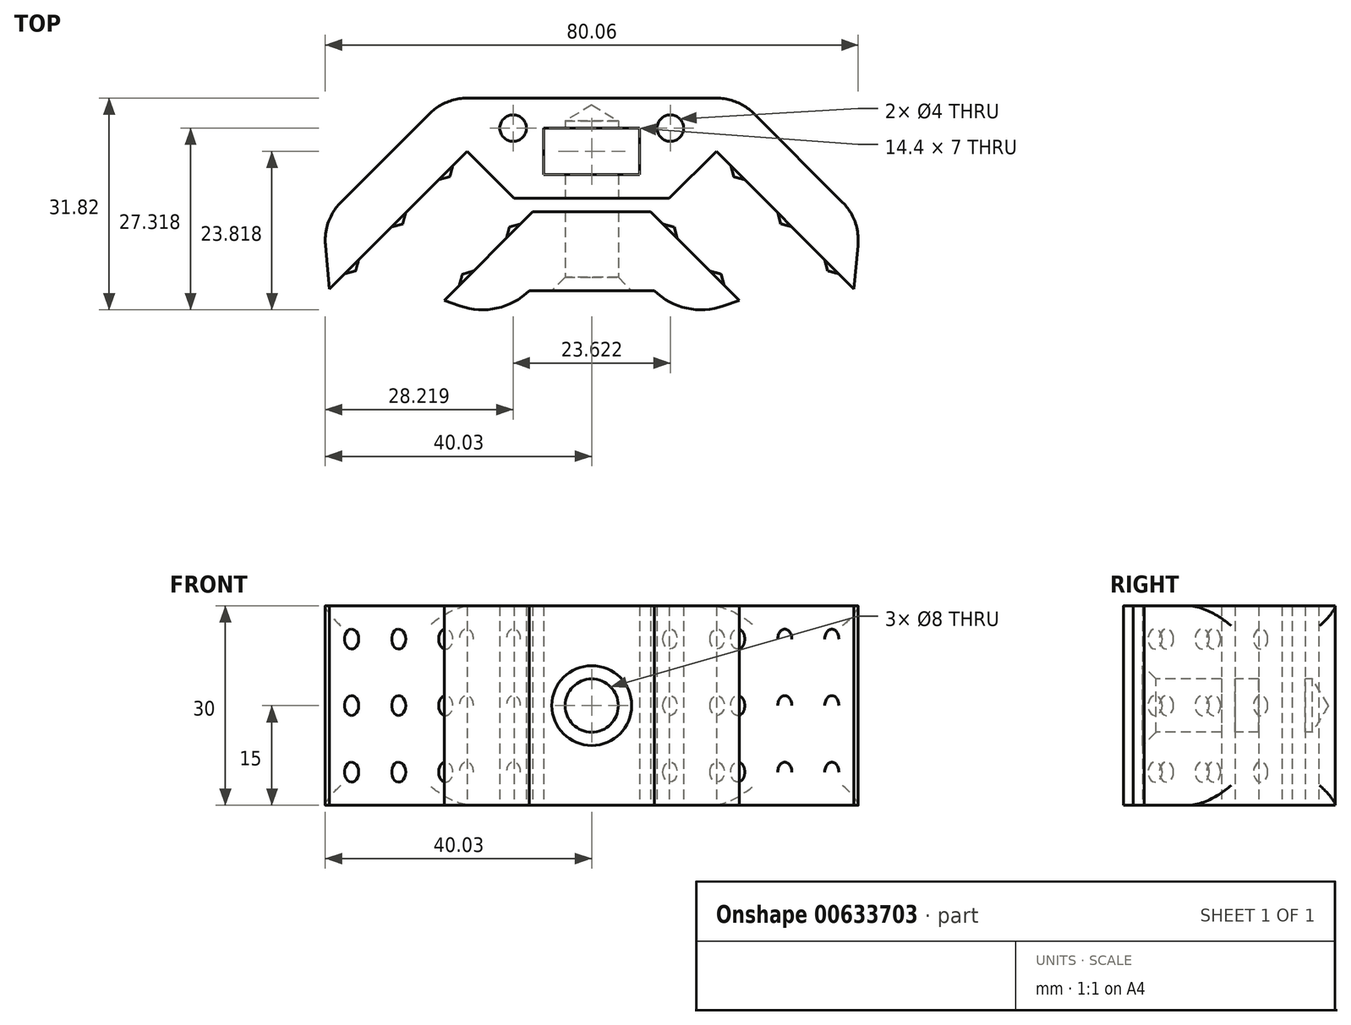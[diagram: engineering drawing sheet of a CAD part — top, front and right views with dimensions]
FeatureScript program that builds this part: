
annotation { "Feature Type Name" : "Feature", "Feature Type Description" : "" }
export const myFeature = defineFeature(function(context is Context, id is Id, definition is map)
    precondition{}
    {
        {
            var Q0;
            Q0=qCreatedBy(makeId("Top.planeOp"),FACE);
            var sketch = newSketch(context, id + "F0", { "sketchPlane" : qUnion([Q0])});
            skLineSegment(sketch, "E0", {"start": v(-6, 0) * mm, "end": v(6, 0) * mm, "construction": true});
            skLineSegment(sketch, "E1.bottom", {"start": v(6, 0) * mm, "end": v(8.87, -2.87) * mm, "construction": true});
            skLineSegment(sketch, "E1.top", {"start": v(18.73, 12.73) * mm, "end": v(89.44, -57.98) * mm});
            skLineSegment(sketch, "E1.left", {"start": v(6, 0) * mm, "end": v(11.66, 5.66) * mm, "construction": true});
            skLineSegment(sketch, "E2.bottom", {"start": v(-6, 0) * mm, "end": v(-8.87, -2.87) * mm, "construction": true});
            skLineSegment(sketch, "E2.top", {"start": v(-18.73, 12.73) * mm, "end": v(-89.44, -57.98) * mm});
            skLineSegment(sketch, "E2.left", {"start": v(-6, 0) * mm, "end": v(-11.66, 5.66) * mm, "construction": true});
            skLineSegment(sketch, "E3", {"start": v(0, 0) * mm, "end": v(0, 18.24) * mm, "construction": true});
            skLineSegment(sketch, "E4", {"start": v(-18.73, 12.73) * mm, "end": v(18.73, 12.73) * mm, "construction": true});
            skLineSegment(sketch, "E5.0", {"start": v(22.04, 20.73) * mm, "end": v(95.1, -52.33) * mm});
            skLineSegment(sketch, "E5.1", {"start": v(-22.04, 20.73) * mm, "end": v(22.04, 20.73) * mm});
            skLineSegment(sketch, "E5.2", {"start": v(-22.04, 20.73) * mm, "end": v(-95.1, -52.33) * mm});
            skPoint(sketch, "E6", {"position": v(-40.34, 2.43) * mm});
            skLineSegment(sketch, "E7", {"start": v(-40.34, 2.43) * mm, "end": v(-39.4, -7.94) * mm});
            skLineSegment(sketch, "E8.MirrorCS", {"start": v(40.34, 2.43) * mm, "end": v(39.4, -7.94) * mm});
            skLineSegment(sketch, "E9.0", {"start": v(-2.69, -8) * mm, "end": v(-71.05, -76.37) * mm});
            skLineSegment(sketch, "E9.1", {"start": v(-2.69, -8) * mm, "end": v(2.69, -8) * mm});
            skLineSegment(sketch, "E9.2", {"start": v(2.69, -8) * mm, "end": v(71.05, -76.37) * mm});
            skLineSegment(sketch, "E10", {"start": v(-22.15, -16.15) * mm, "end": v(-13.82, -19.13) * mm});
            skLineSegment(sketch, "E11.MirrorCS", {"start": v(22.15, -16.15) * mm, "end": v(13.82, -19.13) * mm});
            skLineSegment(sketch, "E12", {"start": v(-9.38, -14.7) * mm, "end": v(9.38, -14.7) * mm});
            skLineSegment(sketch, "E13", {"start": v(-11.66, 5.66) * mm, "end": v(11.66, 5.66) * mm});
            skLineSegment(sketch, "E14", {"start": v(-8.87, -2.87) * mm, "end": v(8.87, -2.87) * mm});
            skLineSegment(sketch, "E15.bottom", {"start": v(7.2, 16.23) * mm, "end": v(-7.2, 16.23) * mm});
            skLineSegment(sketch, "E15.top", {"start": v(7.2, 9.23) * mm, "end": v(-7.2, 9.23) * mm});
            skLineSegment(sketch, "E15.left", {"start": v(7.2, 16.23) * mm, "end": v(7.2, 9.23) * mm});
            skLineSegment(sketch, "E15.right", {"start": v(-7.2, 16.23) * mm, "end": v(-7.2, 9.23) * mm});
            skPoint(sketch, "E15.middle", {"position": v(0, 12.73) * mm});
            skCircle(sketch, "E16", {"center": v(-11.81, 16.23) * mm, "radius": 2 * mm});
            skCircle(sketch, "E17.MirrorC", {"center": v(11.81, 16.23) * mm, "radius": 2 * mm});
            skLineSegment(sketch, "E18", {"start": v(-11.66, 5.66) * mm, "end": v(-18.73, 12.73) * mm});
            skLineSegment(sketch, "E19", {"start": v(-8.87, -2.87) * mm, "end": v(-76.71, -70.71) * mm});
            skLineSegment(sketch, "E20", {"start": v(8.87, -2.87) * mm, "end": v(76.71, -70.71) * mm});
            skLineSegment(sketch, "E21", {"start": v(11.66, 5.66) * mm, "end": v(18.73, 12.73) * mm});
            skSolve(sketch);
        }
        {
            var Q0;
            {var subQ9=sQuery(id+"F0.wireOp",EDGE,"E5.1");Q0=makeQuery(id+"F0.imprint","IMPRINT",FACE,{"disambiguationData":[TD([[makeQuery(id+"F0.imprint","IMPRINT",EDGE,{"derivedFrom":subQ9}),-1.0]])]});}
            var Q1;
            {var subQ0=sQuery(id+"F0.wireOp",EDGE,"E10");Q1=makeQuery(id+"F0.imprint","IMPRINT",FACE,{"disambiguationData":[TD([[makeQuery(id+"F0.imprint","IMPRINT",EDGE,{"derivedFrom":subQ0}),1.0]])]});}
            var Q2;
            {var subQ0=sQuery(id+"F0.wireOp",EDGE,"E9.1");Q2=makeQuery(id+"F0.imprint","IMPRINT",FACE,{"disambiguationData":[TD([[makeQuery(id+"F0.imprint","IMPRINT",EDGE,{"derivedFrom":subQ0}),-1.0]])]});}
            extrude(context, id + "F1", {"entities" : qUnion([Q0, Q1, Q2]), "depth" : 30 * mm, "offsetDistance" : 25 * mm});
        }
        {
            var Q0;
            Q0=makeQuery(id+"F1.opExtrude","SWEPT_FACE",FACE,{"disambiguationData":[OSD([sQuery(id+"F0.wireOp",EDGE,"E12")])]});
            var sketch = newSketch(context, id + "F2", { "sketchPlane" : qUnion([Q0])});
            skPoint(sketch, "E22", {"position": v(0, 15) * mm});
            skPoint(sketch, "E22.positionSnap0", {"position": v(0, 30) * mm});
            skPoint(sketch, "E22.positionSnap1", {"position": v(-9.38, 15) * mm});
            skSolve(sketch);
        }
        {
            var Q0;
            Q0=sQuery(id+"F2.wireOp",VERTEX,"E22");
            var Q1;
            Q1=makeQuery(id+"F1.opExtrude","SWEPT_BODY",BODY,{"disambiguationData":[OSD([sQuery(id+"F0.wireOp",EDGE,"E1.top"),sQuery(id+"F0.wireOp",EDGE,"E2.top"),sQuery(id+"F0.wireOp",EDGE,"E5.0"),sQuery(id+"F0.wireOp",EDGE,"E5.1"),sQuery(id+"F0.wireOp",EDGE,"E5.2"),sQuery(id+"F0.wireOp",EDGE,"E7"),sQuery(id+"F0.wireOp",EDGE,"E8.MirrorCS"),sQuery(id+"F0.wireOp",EDGE,"E13"),sQuery(id+"F0.wireOp",EDGE,"E15.bottom"),sQuery(id+"F0.wireOp",EDGE,"E15.top"),sQuery(id+"F0.wireOp",EDGE,"E15.left"),sQuery(id+"F0.wireOp",EDGE,"E15.right"),sQuery(id+"F0.wireOp",EDGE,"E16"),sQuery(id+"F0.wireOp",EDGE,"E17.MirrorC"),sQuery(id+"F0.wireOp",EDGE,"E18"),sQuery(id+"F0.wireOp",EDGE,"E21")])]});
            var Q2;
            Q2=makeQuery(id+"F1.opExtrude","SWEPT_BODY",BODY,{"disambiguationData":[OSD([sQuery(id+"F0.wireOp",EDGE,"E9.0"),sQuery(id+"F0.wireOp",EDGE,"E9.2"),sQuery(id+"F0.wireOp",EDGE,"E10"),sQuery(id+"F0.wireOp",EDGE,"E11.MirrorCS"),sQuery(id+"F0.wireOp",EDGE,"E12"),sQuery(id+"F0.wireOp",EDGE,"E14"),sQuery(id+"F0.wireOp",EDGE,"E19"),sQuery(id+"F0.wireOp",EDGE,"E20")])]});
            hole(context, id + "F3", {"style" : HoleStyle.C_SINK, "endStyle" : HoleEndStyle.BLIND, "holeDiameter" : 8 * mm, "cSinkDiameter" : 12 * mm, "cSinkAngle" : 90 * degree, "majorDiameter" : 5 * mm, "holeDepth" : 32 * mm, "isTappedThrough" : true, "tappedDepth" : 12 * mm, "tapClearance" : 3, "startFromSketch" : true, "locations" : qUnion([Q0]), "scope" : qUnion([Q1, Q2])});
        }
        {
            var Q0;
            Q0=makeQuery(id+"F1.opExtrude","SWEPT_EDGE",EDGE,{"disambiguationData":[OSD([sQuery(id+"F0.wireOp",EDGE,"E5.2"),sQuery(id+"F0.wireOp",EDGE,"E7")])]});
            var Q1;
            Q1=makeQuery(id+"F1.opExtrude","SWEPT_EDGE",EDGE,{"disambiguationData":[OSD([sQuery(id+"F0.wireOp",EDGE,"E5.1"),sQuery(id+"F0.wireOp",EDGE,"E5.2")])]});
            var Q2;
            Q2=makeQuery(id+"F1.opExtrude","SWEPT_EDGE",EDGE,{"disambiguationData":[OSD([sQuery(id+"F0.wireOp",EDGE,"E5.0"),sQuery(id+"F0.wireOp",EDGE,"E5.1")])]});
            var Q3;
            Q3=makeQuery(id+"F1.opExtrude","SWEPT_EDGE",EDGE,{"disambiguationData":[OSD([sQuery(id+"F0.wireOp",EDGE,"E5.0"),sQuery(id+"F0.wireOp",EDGE,"E8.MirrorCS")])]});
            fillet(context, id + "F4", {"entities" : qUnion([Q0, Q1, Q2, Q3]), "radius" : 8 * mm, "tangentPropagation" : true, "allowEdgeOverflow" : false});
        }
        {
            var Q0;
            Q0=makeQuery(id+"F1.opExtrude","CAP_EDGE",EDGE,{"disambiguationData":[OSD([sQuery(id+"F0.wireOp",EDGE,"E5.0")])],"isStart":false});
            var Q1;
            Q1=makeQuery(id+"F1.opExtrude","CAP_EDGE",EDGE,{"disambiguationData":[OSD([sQuery(id+"F0.wireOp",EDGE,"E5.2")])],"isStart":false});
            var Q2;
            Q2=makeQuery(id+"F1.opExtrude","CAP_EDGE",EDGE,{"disambiguationData":[OSD([sQuery(id+"F0.wireOp",EDGE,"E5.0")])],"isStart":true});
            var Q3;
            Q3=makeQuery(id+"F1.opExtrude","CAP_EDGE",EDGE,{"disambiguationData":[OSD([sQuery(id+"F0.wireOp",EDGE,"E5.2")])],"isStart":true});
            fillet(context, id + "F5", {"entities" : qUnion([Q0, Q1, Q2, Q3]), "radius" : 3 * mm, "allowEdgeOverflow" : false});
        }
        {
            var Q0;
            Q0=makeQuery(id+"F1.opExtrude","SWEPT_EDGE",EDGE,{"disambiguationData":[OSD([sQuery(id+"F0.wireOp",EDGE,"E9.0"),sQuery(id+"F0.wireOp",EDGE,"E10")])]});
            var Q1;
            Q1=makeQuery(id+"F1.opExtrude","SWEPT_EDGE",EDGE,{"disambiguationData":[OSD([sQuery(id+"F0.wireOp",EDGE,"E9.2"),sQuery(id+"F0.wireOp",EDGE,"E11.MirrorCS")])]});
            fillet(context, id + "F6", {"entities" : qUnion([Q0, Q1]), "radius" : 10 * mm, "tangentPropagation" : true, "allowEdgeOverflow" : false});
        }
        {
            var Q0;
            Q0=makeQuery(id+"F1.opExtrude","SWEPT_FACE",FACE,{"disambiguationData":[OSD([sQuery(id+"F0.wireOp",EDGE,"E2.top")])]});
            var sketch = newSketch(context, id + "F7", { "sketchPlane" : qUnion([Q0])});
            skCircle(sketch, "E23", {"center": v(-28.78, 25) * mm, "radius": 1.5 * mm});
            skCircle(sketch, "E24.0.1.0", {"center": v(-28.78, 15) * mm, "radius": 1.5 * mm});
            skCircle(sketch, "E24.0.2.0", {"center": v(-28.78, 5) * mm, "radius": 1.5 * mm});
            skCircle(sketch, "E24.1.0.0", {"center": v(-18.78, 25) * mm, "radius": 1.5 * mm});
            skCircle(sketch, "E24.1.1.0", {"center": v(-18.78, 15) * mm, "radius": 1.5 * mm});
            skCircle(sketch, "E24.1.2.0", {"center": v(-18.78, 5) * mm, "radius": 1.5 * mm});
            skCircle(sketch, "E24.2.0.0", {"center": v(-8.78, 25) * mm, "radius": 1.5 * mm});
            skCircle(sketch, "E24.2.1.0", {"center": v(-8.78, 15) * mm, "radius": 1.5 * mm});
            skCircle(sketch, "E24.2.2.0", {"center": v(-8.78, 5) * mm, "radius": 1.5 * mm});
            skLineSegment(sketch, "E24.direction1", {"start": v(-28.78, 25) * mm, "end": v(-18.78, 25) * mm, "construction": true});
            skLineSegment(sketch, "E24.direction2", {"start": v(-28.78, 25) * mm, "end": v(-28.78, 15) * mm, "construction": true});
            skLineSegment(sketch, "E25", {"start": v(-28.78, 25) * mm, "end": v(-33.48, 25) * mm, "construction": true});
            skLineSegment(sketch, "E26", {"start": v(-28.78, 25) * mm, "end": v(-28.78, 30) * mm, "construction": true});
            skSolve(sketch);
        }
        {
            var Q0;
            Q0=makeQuery(id+"F1.opExtrude","SWEPT_FACE",FACE,{"disambiguationData":[OSD([sQuery(id+"F0.wireOp",EDGE,"E1.top")])]});
            var sketch = newSketch(context, id + "F8", { "sketchPlane" : qUnion([Q0])});
            skCircle(sketch, "E27", {"center": v(8.78, 25) * mm, "radius": 1.5 * mm});
            skCircle(sketch, "E28.0.1.0", {"center": v(8.78, 15) * mm, "radius": 1.5 * mm});
            skCircle(sketch, "E28.0.2.0", {"center": v(8.78, 5) * mm, "radius": 1.5 * mm});
            skCircle(sketch, "E28.1.0.0", {"center": v(18.78, 25) * mm, "radius": 1.5 * mm});
            skCircle(sketch, "E28.1.1.0", {"center": v(18.78, 15) * mm, "radius": 1.5 * mm});
            skCircle(sketch, "E28.1.2.0", {"center": v(18.78, 5) * mm, "radius": 1.5 * mm});
            skCircle(sketch, "E28.2.0.0", {"center": v(28.78, 25) * mm, "radius": 1.5 * mm});
            skCircle(sketch, "E28.2.1.0", {"center": v(28.78, 15) * mm, "radius": 1.5 * mm});
            skCircle(sketch, "E28.2.2.0", {"center": v(28.78, 5) * mm, "radius": 1.5 * mm});
            skLineSegment(sketch, "E28.direction1", {"start": v(8.78, 25) * mm, "end": v(18.78, 25) * mm, "construction": true});
            skLineSegment(sketch, "E28.direction2", {"start": v(8.78, 25) * mm, "end": v(8.78, 15) * mm, "construction": true});
            skLineSegment(sketch, "E29", {"start": v(28.78, 25) * mm, "end": v(33.48, 25) * mm, "construction": true});
            skLineSegment(sketch, "E30", {"start": v(33.48, 25) * mm, "end": v(28.78, 25) * mm, "construction": true});
            skLineSegment(sketch, "E31", {"start": v(28.78, 25) * mm, "end": v(28.78, 30) * mm, "construction": true});
            skSolve(sketch);
        }
        {
            var Q0;
            Q0=makeQuery(id+"F1.opExtrude","SWEPT_FACE",FACE,{"disambiguationData":[OSD([sQuery(id+"F0.wireOp",EDGE,"E19")])]});
            var sketch = newSketch(context, id + "F9", { "sketchPlane" : qUnion([Q0])});
            skCircle(sketch, "E32", {"center": v(12.39, 25) * mm, "radius": 1.5 * mm});
            skCircle(sketch, "E33.0.1.0", {"center": v(12.39, 15) * mm, "radius": 1.5 * mm});
            skCircle(sketch, "E33.0.2.0", {"center": v(12.39, 5) * mm, "radius": 1.5 * mm});
            skCircle(sketch, "E33.1.0.0", {"center": v(22.39, 25) * mm, "radius": 1.5 * mm});
            skCircle(sketch, "E33.1.1.0", {"center": v(22.39, 15) * mm, "radius": 1.5 * mm});
            skCircle(sketch, "E33.1.2.0", {"center": v(22.39, 5) * mm, "radius": 1.5 * mm});
            skLineSegment(sketch, "E33.direction1", {"start": v(12.39, 25) * mm, "end": v(22.39, 25) * mm, "construction": true});
            skLineSegment(sketch, "E33.direction2", {"start": v(12.39, 25) * mm, "end": v(12.39, 15) * mm, "construction": true});
            skLineSegment(sketch, "E34", {"start": v(22.39, 25) * mm, "end": v(22.39, 30) * mm, "construction": true});
            skLineSegment(sketch, "E35", {"start": v(22.39, 25) * mm, "end": v(27.09, 25) * mm, "construction": true});
            skSolve(sketch);
        }
        {
            var Q0;
            Q0=makeQuery(id+"F1.opExtrude","SWEPT_FACE",FACE,{"disambiguationData":[OSD([sQuery(id+"F0.wireOp",EDGE,"E20")])]});
            var sketch = newSketch(context, id + "F10", { "sketchPlane" : qUnion([Q0])});
            skCircle(sketch, "E36", {"center": v(-22.39, 25) * mm, "radius": 1.5 * mm});
            skCircle(sketch, "E37.0.1.0", {"center": v(-22.39, 15) * mm, "radius": 1.5 * mm});
            skCircle(sketch, "E37.0.2.0", {"center": v(-22.39, 5) * mm, "radius": 1.5 * mm});
            skCircle(sketch, "E37.1.0.0", {"center": v(-12.39, 25) * mm, "radius": 1.5 * mm});
            skCircle(sketch, "E37.1.1.0", {"center": v(-12.39, 15) * mm, "radius": 1.5 * mm});
            skCircle(sketch, "E37.1.2.0", {"center": v(-12.39, 5) * mm, "radius": 1.5 * mm});
            skLineSegment(sketch, "E37.direction1", {"start": v(-22.39, 25) * mm, "end": v(-12.39, 25) * mm, "construction": true});
            skLineSegment(sketch, "E37.direction2", {"start": v(-22.39, 25) * mm, "end": v(-22.39, 15) * mm, "construction": true});
            skLineSegment(sketch, "E38", {"start": v(-22.39, 25) * mm, "end": v(-27.09, 25) * mm});
            skLineSegment(sketch, "E39", {"start": v(-27.09, 25) * mm, "end": v(-22.39, 25) * mm, "construction": true});
            skLineSegment(sketch, "E40", {"start": v(-22.39, 25) * mm, "end": v(-22.39, 30) * mm, "construction": true});
            skSolve(sketch);
        }
        {
            var Q0;
            Q0 = qSketchRegion(id + "F9", true);
            extrude(context, id + "F11", {"entities" : qUnion([Q0]), "operationType" : NewBodyOperationType.ADD, "depth" : 1 * mm, "offsetDistance" : 25 * mm, "hasDraft" : true, "draftAngle" : 60 * degree, "draftPullDirection" : true});
        }
        {
            var Q0;
            Q0 = qSketchRegion(id + "F7", true);
            extrude(context, id + "F12", {"entities" : qUnion([Q0]), "operationType" : NewBodyOperationType.ADD, "depth" : 1 * mm, "offsetDistance" : 25 * mm, "hasDraft" : true, "draftAngle" : 60 * degree, "draftPullDirection" : true});
        }
        {
            var Q0;
            Q0 = qSketchRegion(id + "F8", true);
            extrude(context, id + "F13", {"entities" : qUnion([Q0]), "operationType" : NewBodyOperationType.ADD, "depth" : 1 * mm, "offsetDistance" : 25 * mm, "hasDraft" : true, "draftAngle" : 60 * degree, "draftPullDirection" : true});
        }
        {
            var Q0;
            Q0 = qSketchRegion(id + "F10", true);
            extrude(context, id + "F14", {"entities" : qUnion([Q0]), "operationType" : NewBodyOperationType.ADD, "depth" : 1 * mm, "offsetDistance" : 25 * mm, "hasDraft" : true, "draftAngle" : 60 * degree, "draftPullDirection" : true});
        }
        {
            var Q0;
            Q0=makeQuery(id+"F1.opExtrude","SWEPT_BODY",BODY,{"disambiguationData":[OSD([sQuery(id+"F0.wireOp",EDGE,"E9.0"),sQuery(id+"F0.wireOp",EDGE,"E9.2"),sQuery(id+"F0.wireOp",EDGE,"E10"),sQuery(id+"F0.wireOp",EDGE,"E11.MirrorCS"),sQuery(id+"F0.wireOp",EDGE,"E12"),sQuery(id+"F0.wireOp",EDGE,"E14"),sQuery(id+"F0.wireOp",EDGE,"E19"),sQuery(id+"F0.wireOp",EDGE,"E20")])]});
            transform(context, id + "F15", {"entities" : qUnion([Q0]), "transformType" : TransformType.TRANSLATION_3D, "dx" : 0 * mm, "dy" : 6.5 * mm, "dz" : 0 * mm, "makeCopy" : false});
        }
    });
